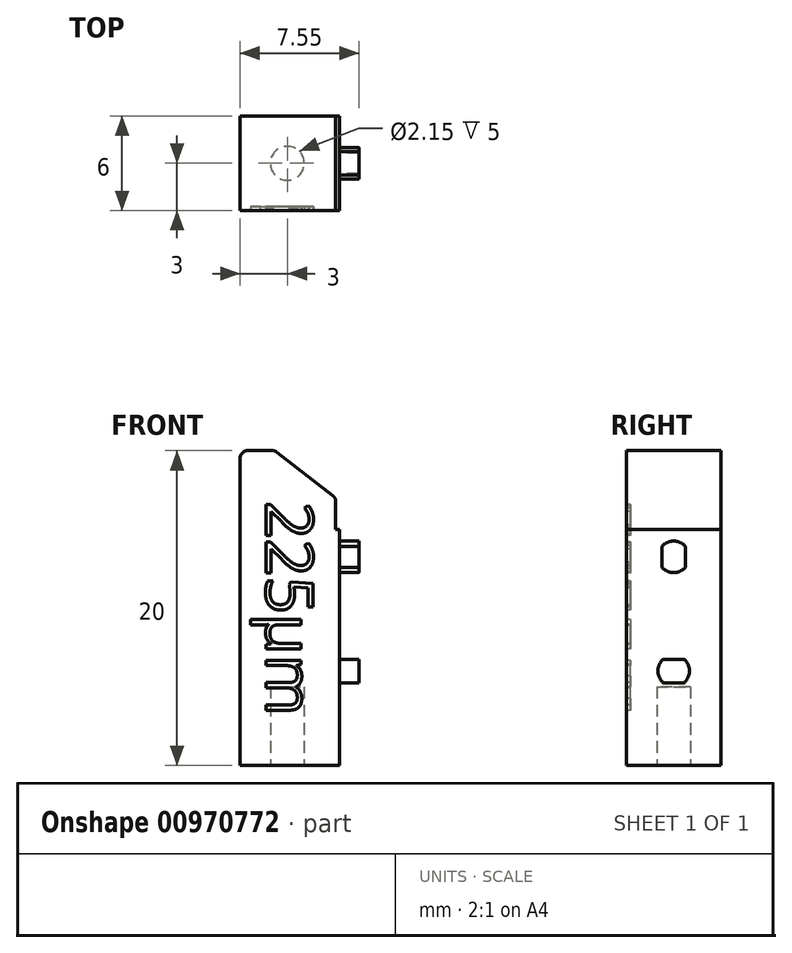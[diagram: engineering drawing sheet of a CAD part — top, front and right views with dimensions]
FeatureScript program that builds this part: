
annotation { "Feature Type Name" : "Feature", "Feature Type Description" : "" }
export const myFeature = defineFeature(function(context is Context, id is Id, definition is map)
    precondition{}
    {
        {
            var Q0;
            Q0=qCreatedBy(makeId("Front.planeOp"),FACE);
            var sketch = newSketch(context, id + "F0", { "sketchPlane" : qUnion([Q0])});
            skLineSegment(sketch, "E0.bottom", {"start": v(-0.93, 10) * mm, "end": v(-3.15, 10) * mm});
            skLineSegment(sketch, "E0.top", {"start": v(3.15, -10) * mm, "end": v(-3.15, -10) * mm});
            skLineSegment(sketch, "E0.left", {"start": v(3.15, 5) * mm, "end": v(3.15, -10) * mm});
            skLineSegment(sketch, "E0.right", {"start": v(-3.15, 10) * mm, "end": v(-3.15, -10) * mm});
            skPoint(sketch, "E0.middle", {"position": v(0, 0) * mm});
            skLineSegment(sketch, "E1", {"start": v(3.15, 5) * mm, "end": v(2.92, 5) * mm});
            skLineSegment(sketch, "E2", {"start": v(2.92, 5) * mm, "end": v(2.92, 7) * mm});
            skLineSegment(sketch, "E3", {"start": v(2.92, 7) * mm, "end": v(-0.93, 10) * mm});
            skPoint(sketch, "E4.orphan", {"position": v(3.15, 10) * mm});
            skSolve(sketch);
        }
        {
            var Q0;
            Q0 = qSketchRegion(id + "F0", true);
            extrude(context, id + "F1", {"entities" : qUnion([Q0]), "depth" : 6 * mm, "offsetDistance" : 25 * mm});
        }
        {
            var Q0;
            Q0=makeQuery(id+"F1.opExtrude","SWEPT_FACE",FACE,{"disambiguationData":[OSD([sQuery(id+"F0.wireOp",EDGE,"E0.left")])]});
            var sketch = newSketch(context, id + "F2", { "sketchPlane" : qUnion([Q0])});
            skLineSegment(sketch, "E5", {"start": v(-3, 5) * mm, "end": v(-3, -10) * mm, "construction": true});
            skLineSegment(sketch, "E6", {"start": v(-6, 3.25) * mm, "end": v(0, 3.25) * mm, "construction": true});
            skLineSegment(sketch, "E7", {"start": v(0, -4) * mm, "end": v(-6, -4) * mm, "construction": true});
            skArc(sketch, "E8", {"start": v(-3.66, -3.25) * mm, "mid": v(-4, -4) * mm, "end": v(-3.66, -4.75) * mm});
            skArc(sketch, "E9", {"start": v(-3.75, 2.59) * mm, "mid": v(-3, 2.25) * mm, "end": v(-2.25, 2.59) * mm});
            skLineSegment(sketch, "E10.bottom", {"start": v(-2.25, 1.82) * mm, "end": v(-3.75, 1.82) * mm, "construction": true});
            skLineSegment(sketch, "E10.top", {"start": v(-2.25, 4.68) * mm, "end": v(-3.75, 4.68) * mm, "construction": true});
            skLineSegment(sketch, "E10.left", {"start": v(-2.25, 1.82) * mm, "end": v(-2.25, 4.68) * mm, "construction": true});
            skLineSegment(sketch, "E10.right", {"start": v(-3.75, 1.82) * mm, "end": v(-3.75, 4.68) * mm, "construction": true});
            skLineSegment(sketch, "E11.bottom", {"start": v(-4.43, -4.75) * mm, "end": v(-1.57, -4.75) * mm, "construction": true});
            skLineSegment(sketch, "E11.top", {"start": v(-4.43, -3.25) * mm, "end": v(-1.57, -3.25) * mm, "construction": true});
            skLineSegment(sketch, "E11.left", {"start": v(-4.43, -4.75) * mm, "end": v(-4.43, -3.25) * mm, "construction": true});
            skLineSegment(sketch, "E11.right", {"start": v(-1.57, -4.75) * mm, "end": v(-1.57, -3.25) * mm, "construction": true});
            skArc(sketch, "E12.trimOffspring", {"start": v(-2.25, 3.91) * mm, "mid": v(-3, 4.25) * mm, "end": v(-3.75, 3.91) * mm});
            skArc(sketch, "E13.trimOffspring", {"start": v(-2.34, -4.75) * mm, "mid": v(-2, -4) * mm, "end": v(-2.34, -3.25) * mm});
            skLineSegment(sketch, "E14", {"start": v(-3.66, -3.25) * mm, "end": v(-2.34, -3.25) * mm});
            skLineSegment(sketch, "E15", {"start": v(-2.34, -4.75) * mm, "end": v(-3.66, -4.75) * mm});
            skLineSegment(sketch, "E16", {"start": v(-2.25, 2.59) * mm, "end": v(-2.25, 3.91) * mm});
            skLineSegment(sketch, "E17", {"start": v(-3.75, 3.91) * mm, "end": v(-3.75, 2.59) * mm});
            skSolve(sketch);
        }
        {
            var Q0;
            Q0 = qSketchRegion(id + "F2", true);
            extrude(context, id + "F3", {"entities" : qUnion([Q0]), "operationType" : NewBodyOperationType.ADD, "depth" : 1.25 * mm, "offsetDistance" : 25 * mm});
        }
        {
            var Q0;
            Q0=makeQuery(id+"F1.opExtrude","SWEPT_FACE",FACE,{"disambiguationData":[OSD([sQuery(id+"F0.wireOp",EDGE,"E0.top")])]});
            var sketch = newSketch(context, id + "F4", { "sketchPlane" : qUnion([Q0])});
            skLineSegment(sketch, "E18", {"start": v(-3.15, 3) * mm, "end": v(3.15, 3) * mm, "construction": true});
            skCircle(sketch, "E19", {"center": v(-0.15, 3) * mm, "radius": 1.07 * mm});
            skSolve(sketch);
        }
        {
            var Q0;
            Q0 = qSketchRegion(id + "F4", true);
            extrude(context, id + "F5", {"entities" : qUnion([Q0]), "operationType" : NewBodyOperationType.REMOVE, "oppositeDirection" : true, "depth" : 5 * mm, "offsetDistance" : 25 * mm});
        }
        {
            var Q0;
            Q0=makeQuery(id+"F1.opExtrude","SWEPT_EDGE",EDGE,{"disambiguationData":[OSD([sQuery(id+"F0.wireOp",EDGE,"E2"),sQuery(id+"F0.wireOp",EDGE,"E3")])]});
            var Q1;
            Q1=makeQuery(id+"F1.opExtrude","SWEPT_EDGE",EDGE,{"disambiguationData":[OSD([sQuery(id+"F0.wireOp",EDGE,"E0.bottom"),sQuery(id+"F0.wireOp",EDGE,"E3")])]});
            var Q2;
            Q2=makeQuery(id+"F1.opExtrude","SWEPT_EDGE",EDGE,{"disambiguationData":[OSD([sQuery(id+"F0.wireOp",EDGE,"E0.bottom"),sQuery(id+"F0.wireOp",EDGE,"E0.right")])]});
            fillet(context, id + "F6", {"entities" : qUnion([Q0, Q1, Q2]), "radius" : .5 * mm, "tangentPropagation" : true, "allowEdgeOverflow" : false});
        }
        {
            var Q0;
            Q0=makeQuery(id+"F1.opExtrude","CAP_FACE",FACE,{"disambiguationData":[OSD([sQuery(id+"F0.wireOp",EDGE,"E0.bottom"),sQuery(id+"F0.wireOp",EDGE,"E0.top"),sQuery(id+"F0.wireOp",EDGE,"E0.left"),sQuery(id+"F0.wireOp",EDGE,"E0.right"),sQuery(id+"F0.wireOp",EDGE,"E1"),sQuery(id+"F0.wireOp",EDGE,"E2"),sQuery(id+"F0.wireOp",EDGE,"E3")])],"isStart":false});
            var sketch = newSketch(context, id + "F7", { "sketchPlane" : qUnion([Q0])});
            skLineSegment(sketch, "E20.bottom", {"start": v(-1.5, -6.77) * mm, "end": v(1.5, -6.77) * mm, "construction": true});
            skLineSegment(sketch, "E20.top", {"start": v(-1.5, 6.77) * mm, "end": v(1.5, 6.77) * mm, "construction": true});
            skLineSegment(sketch, "E20.left", {"start": v(-1.5, -6.77) * mm, "end": v(-1.5, 4.45) * mm, "construction": true});
            skLineSegment(sketch, "E20.right", {"start": v(1.5, -6.77) * mm, "end": v(1.5, 6.77) * mm, "construction": true});
            skPoint(sketch, "E20.middle", {"position": v(0, 0) * mm});
            skText(sketch, "E21", { "text": "225µm", "fontName": "OpenSans-Regular.ttf"});
            const initialGuessF7  = {"E21": [-0.0015, 0.00677, 0, -1, 0.003]};
            skSetInitialGuess(sketch, initialGuessF7);
            skSolve(sketch);
        }
        {
            var Q0;
            Q0 = qSketchRegion(id + "F7", true);
            extrude(context, id + "F8", {"entities" : qUnion([Q0]), "operationType" : NewBodyOperationType.REMOVE, "oppositeDirection" : true, "depth" : .25 * mm, "offsetDistance" : 25 * mm});
        }
    });
